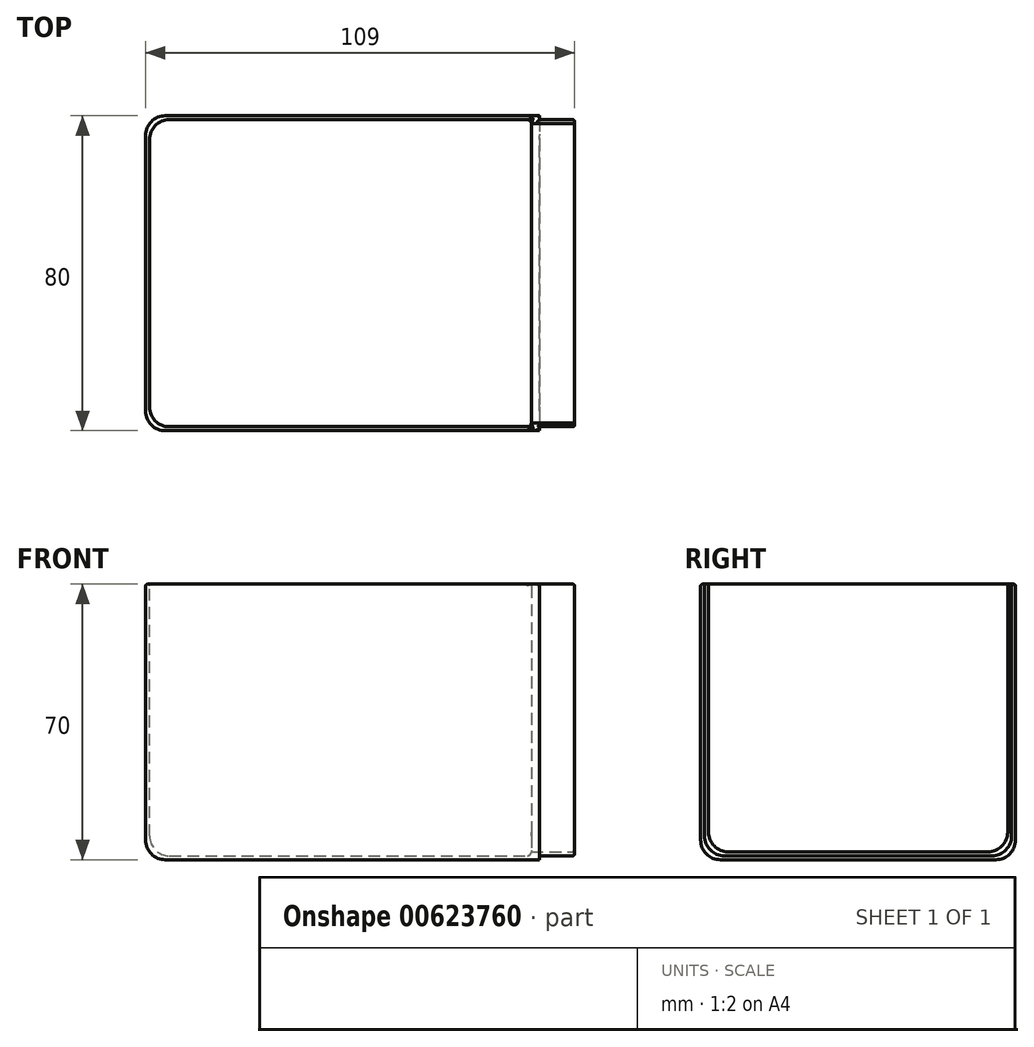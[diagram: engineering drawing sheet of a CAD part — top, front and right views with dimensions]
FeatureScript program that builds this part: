
annotation { "Feature Type Name" : "Feature", "Feature Type Description" : "" }
export const myFeature = defineFeature(function(context is Context, id is Id, definition is map)
    precondition{}
    {
        {
            var Q0;
            Q0=qCreatedBy(makeId("Top.planeOp"),FACE);
            var sketch = newSketch(context, id + "F0", { "sketchPlane" : qUnion([Q0])});
            skLineSegment(sketch, "E0.bottom", {"start": v(50, -40) * mm, "end": v(-50, -40) * mm});
            skLineSegment(sketch, "E0.top", {"start": v(50, 40) * mm, "end": v(-50, 40) * mm});
            skLineSegment(sketch, "E0.left", {"start": v(50, -40) * mm, "end": v(50, 40) * mm});
            skLineSegment(sketch, "E0.right", {"start": v(-50, -40) * mm, "end": v(-50, 40) * mm});
            skPoint(sketch, "E0.middle", {"position": v(0, 0) * mm});
            skSolve(sketch);
        }
        {
            var Q0;
            Q0=makeQuery(id+"F0.imprint","IMPRINT",FACE,{"disambiguationData":[TD([[makeQuery(id+"F0.imprint","IMPRINT",EDGE,{"derivedFrom":sQuery(id+"F0.wireOp",EDGE,"E0.bottom")}),-1.0]])]});
            extrude(context, id + "F1", {"entities" : qUnion([Q0]), "depth" : 70 * mm, "offsetDistance" : 25 * mm});
        }
        {
            var Q0;
            Q0=makeQuery(id+"F1.opExtrude","CAP_FACE",FACE,{"disambiguationData":[OSD([sQuery(id+"F0.wireOp",EDGE,"E0.bottom"),sQuery(id+"F0.wireOp",EDGE,"E0.top"),sQuery(id+"F0.wireOp",EDGE,"E0.left"),sQuery(id+"F0.wireOp",EDGE,"E0.right")])],"isStart":false});
            var sketch = newSketch(context, id + "F2", { "sketchPlane" : qUnion([Q0])});
            skLineSegment(sketch, "E1.bottom", {"start": v(-49, 39) * mm, "end": v(48, 39) * mm});
            skLineSegment(sketch, "E1.top", {"start": v(-49, -39) * mm, "end": v(48, -39) * mm});
            skLineSegment(sketch, "E1.left", {"start": v(-49, 39) * mm, "end": v(-49, -39) * mm});
            skLineSegment(sketch, "E1.right", {"start": v(48, 39) * mm, "end": v(48, -39) * mm});
            skLineSegment(sketch, "E2", {"start": v(-50, 20.59) * mm, "end": v(-49, 20.59) * mm});
            skLineSegment(sketch, "E3", {"start": v(-70.41, 40) * mm, "end": v(-70.41, 39) * mm});
            skLineSegment(sketch, "E4", {"start": v(-57.73, -39) * mm, "end": v(-57.73, -40) * mm});
            skLineSegment(sketch, "E5", {"start": v(48, -31.07) * mm, "end": v(50, -31.07) * mm});
            skSolve(sketch);
        }
        {
            var Q0;
            {var subQ4=sQuery(id+"F2.wireOp",EDGE,"E1.left");var subQ6=sQuery(id+"F2.wireOp",EDGE,"E1.bottom");var subQ9=makeQuery(id+"F2.imprint","INTERSECT",VERTEX,{"derivedFrom":[subQ6,subQ4]});Q0=makeQuery(id+"F2.imprint","IMPRINT",FACE,{"disambiguationData":[TD([[makeQuery(id+"F2.imprint","IMPRINT",EDGE,{"disambiguationData":[TD([[subQ9,-1.0]])],"derivedFrom":subQ6}),-1.0]])]});}
            extrude(context, id + "F3", {"entities" : qUnion([Q0]), "operationType" : NewBodyOperationType.REMOVE, "oppositeDirection" : true, "depth" : 69 * mm, "offsetDistance" : 25 * mm});
        }
        {
            var Q0;
            Q0=makeQuery(id+"F1.opExtrude","SWEPT_FACE",FACE,{"disambiguationData":[OSD([sQuery(id+"F0.wireOp",EDGE,"E0.left")])]});
            var sketch = newSketch(context, id + "F4", { "sketchPlane" : qUnion([Q0])});
            skLineSegment(sketch, "E6.bottom", {"start": v(38, 70) * mm, "end": v(-38, 70) * mm});
            skLineSegment(sketch, "E6.top", {"start": v(38, 2) * mm, "end": v(-38, 2) * mm});
            skLineSegment(sketch, "E6.left", {"start": v(38, 70) * mm, "end": v(38, 2) * mm});
            skLineSegment(sketch, "E6.right", {"start": v(-38, 70) * mm, "end": v(-38, 2) * mm});
            skLineSegment(sketch, "E7", {"start": v(-40, 42.3) * mm, "end": v(-38, 42.3) * mm});
            skSolve(sketch);
        }
        {
            var Q0;
            {var subQ1=sQuery(id+"F4.wireOp",EDGE,"E6.bottom");Q0=makeQuery(id+"F4.imprint","IMPRINT",FACE,{"disambiguationData":[TD([[makeQuery(id+"F4.imprint","IMPRINT",EDGE,{"derivedFrom":subQ1}),-1.0]])]});}
            extrude(context, id + "F5", {"entities" : qUnion([Q0]), "operationType" : NewBodyOperationType.REMOVE, "oppositeDirection" : true, "depth" : 2 * mm, "offsetDistance" : 25 * mm});
        }
        {
            var Q0;
            Q0=makeQuery(id+"F3.boolean.opBoolean","COPY",FACE,{"derivedFrom":makeQuery(id+"F3.opExtrude","SWEPT_FACE",FACE,{"disambiguationData":[OSD([sQuery(id+"F2.wireOp",EDGE,"E1.right")])]})});
            var sketch = newSketch(context, id + "F6", { "sketchPlane" : qUnion([Q0])});
            skSolve(sketch);
        }
        {
            var Q0;
            {var subQ0=sQuery(id+"F2.wireOp",EDGE,"E1.right");Q0=makeQuery(id+"F6.imprint","IMPRINT",FACE,{"disambiguationData":[TD([[makeQuery(id+"F6.imprint","IMPRINT",EDGE,{"derivedFrom":makeQuery(id+"F3.boolean.opBoolean","COPY",EDGE,{"derivedFrom":makeQuery(id+"F3.opExtrude","CAP_EDGE",EDGE,{"disambiguationData":[OSD([subQ0])],"isStart":false})})}),1.0]])]});}
            extrude(context, id + "F7", {"entities" : qUnion([Q0]), "operationType" : NewBodyOperationType.ADD, "oppositeDirection" : true, "depth" : 11 * mm, "offsetDistance" : 25 * mm});
        }
        {
            var Q0;
            Q0=makeQuery(id+"F3.boolean.opBoolean","COPY",EDGE,{"derivedFrom":makeQuery(id+"F3.opExtrude","CAP_EDGE",EDGE,{"disambiguationData":[OSD([sQuery(id+"F2.wireOp",EDGE,"E1.bottom")])],"isStart":false})});
            var Q1;
            Q1=makeQuery(id+"F3.boolean.opBoolean","COPY",EDGE,{"derivedFrom":makeQuery(id+"F3.opExtrude","CAP_EDGE",EDGE,{"disambiguationData":[OSD([sQuery(id+"F2.wireOp",EDGE,"E1.left")])],"isStart":false})});
            var Q2;
            Q2=makeQuery(id+"F3.boolean.opBoolean","COPY",EDGE,{"derivedFrom":makeQuery(id+"F3.opExtrude","CAP_EDGE",EDGE,{"disambiguationData":[OSD([sQuery(id+"F2.wireOp",EDGE,"E1.top")])],"isStart":false})});
            var Q3;
            Q3=makeQuery(id+"F1.opExtrude","CAP_EDGE",EDGE,{"disambiguationData":[OSD([sQuery(id+"F0.wireOp",EDGE,"E0.top")])],"isStart":true});
            var Q4;
            Q4=makeQuery(id+"F1.opExtrude","CAP_EDGE",EDGE,{"disambiguationData":[OSD([sQuery(id+"F0.wireOp",EDGE,"E0.right")])],"isStart":true});
            var Q5;
            Q5=makeQuery(id+"F1.opExtrude","CAP_EDGE",EDGE,{"disambiguationData":[OSD([sQuery(id+"F0.wireOp",EDGE,"E0.bottom")])],"isStart":true});
            var Q6;
            Q6=makeQuery(id+"F1.opExtrude","SWEPT_EDGE",EDGE,{"disambiguationData":[OSD([sQuery(id+"F0.wireOp",EDGE,"E0.bottom"),sQuery(id+"F0.wireOp",EDGE,"E0.right")])]});
            var Q7;
            Q7=makeQuery(id+"F1.opExtrude","SWEPT_EDGE",EDGE,{"disambiguationData":[OSD([sQuery(id+"F0.wireOp",EDGE,"E0.top"),sQuery(id+"F0.wireOp",EDGE,"E0.right")])]});
            var Q8;
            Q8=makeQuery(id+"F3.boolean.opBoolean","COPY",EDGE,{"derivedFrom":makeQuery(id+"F3.opExtrude","SWEPT_EDGE",EDGE,{"disambiguationData":[OSD([sQuery(id+"F2.wireOp",EDGE,"E1.bottom"),sQuery(id+"F2.wireOp",EDGE,"E1.left")])]})});
            var Q9;
            Q9=makeQuery(id+"F3.boolean.opBoolean","COPY",EDGE,{"derivedFrom":makeQuery(id+"F3.opExtrude","SWEPT_EDGE",EDGE,{"disambiguationData":[OSD([sQuery(id+"F2.wireOp",EDGE,"E1.top"),sQuery(id+"F2.wireOp",EDGE,"E1.left")])]})});
            var Q10;
            {var subQ0=sQuery(id+"F2.wireOp",EDGE,"E1.right");var subQ1=sQuery(id+"F2.wireOp",EDGE,"E1.bottom");Q10=makeQuery(id+"F7.opExtrude","SWEPT_EDGE",EDGE,{"disambiguationData":[OSD([subQ1,subQ0]),TDD([makeQuery(id+"F6.imprint","INTERSECT",VERTEX,{"derivedFrom":[makeQuery(id+"F3.boolean.opBoolean","COPY",EDGE,{"derivedFrom":makeQuery(id+"F3.opExtrude","SWEPT_EDGE",EDGE,{"disambiguationData":[OSD([subQ1,subQ0])]})}),makeQuery(id+"F3.boolean.opBoolean","COPY",EDGE,{"derivedFrom":makeQuery(id+"F3.opExtrude","CAP_EDGE",EDGE,{"disambiguationData":[OSD([subQ0])],"isStart":false})})]})])]});}
            var Q11;
            {var subQ0=sQuery(id+"F2.wireOp",EDGE,"E1.right");var subQ1=sQuery(id+"F2.wireOp",EDGE,"E1.top");Q11=makeQuery(id+"F7.opExtrude","SWEPT_EDGE",EDGE,{"disambiguationData":[OSD([subQ1,subQ0]),TDD([makeQuery(id+"F6.imprint","INTERSECT",VERTEX,{"derivedFrom":[makeQuery(id+"F3.boolean.opBoolean","COPY",EDGE,{"derivedFrom":makeQuery(id+"F3.opExtrude","SWEPT_EDGE",EDGE,{"disambiguationData":[OSD([subQ1,subQ0])]})}),makeQuery(id+"F3.boolean.opBoolean","COPY",EDGE,{"derivedFrom":makeQuery(id+"F3.opExtrude","CAP_EDGE",EDGE,{"disambiguationData":[OSD([subQ0])],"isStart":false})})]})])]});}
            var Q12;
            {var subQ0=sQuery(id+"F4.wireOp",EDGE,"E6.right");var subQ1=sQuery(id+"F4.wireOp",EDGE,"E6.top");Q12=makeQuery(id+"F7.boolean.opBoolean","MERGE",EDGE,{"derivedFrom":[makeQuery(id+"F5.boolean.opBoolean","COPY",EDGE,{"derivedFrom":makeQuery(id+"F5.opExtrude","SWEPT_EDGE",EDGE,{"disambiguationData":[OSD([subQ1,subQ0])]})}),makeQuery(id+"F7.opExtrude","SWEPT_EDGE",EDGE,{"disambiguationData":[OSD([subQ1,subQ0])]})]});}
            var Q13;
            {var subQ0=sQuery(id+"F4.wireOp",EDGE,"E6.left");var subQ1=sQuery(id+"F4.wireOp",EDGE,"E6.top");Q13=makeQuery(id+"F7.boolean.opBoolean","MERGE",EDGE,{"derivedFrom":[makeQuery(id+"F5.boolean.opBoolean","COPY",EDGE,{"derivedFrom":makeQuery(id+"F5.opExtrude","SWEPT_EDGE",EDGE,{"disambiguationData":[OSD([subQ1,subQ0])]})}),makeQuery(id+"F7.opExtrude","SWEPT_EDGE",EDGE,{"disambiguationData":[OSD([subQ1,subQ0])]})]});}
            fillet(context, id + "F8", {"entities" : qUnion([Q0, Q1, Q2, Q3, Q4, Q5, Q6, Q7, Q8, Q9, Q10, Q11, Q12, Q13]), "radius" : 5 * mm, "tangentPropagation" : true, "allowEdgeOverflow" : false});
        }
        {
            var Q0;
            {var subQ0=makeQuery(id+"F1.opExtrude","CAP_FACE",FACE,{"disambiguationData":[OSD([sQuery(id+"F0.wireOp",EDGE,"E0.bottom"),sQuery(id+"F0.wireOp",EDGE,"E0.top"),sQuery(id+"F0.wireOp",EDGE,"E0.left"),sQuery(id+"F0.wireOp",EDGE,"E0.right")])],"isStart":false});var subQ1=sQuery(id+"F2.wireOp",EDGE,"E1.right");var subQ3=makeQuery(id+"F3.boolean.opBoolean","COPY",EDGE,{"derivedFrom":makeQuery(id+"F3.opExtrude","CAP_EDGE",EDGE,{"disambiguationData":[OSD([subQ1])],"isStart":true})});Q0=makeQuery(id+"F7.boolean.opBoolean","MERGE",FACE,{"derivedFrom":[subQ0,makeQuery(id+"F7.opExtrude","SWEPT_FACE",FACE,{"disambiguationData":[OSD([subQ1]),TDD([makeQuery(id+"F6.imprint","IMPRINT",EDGE,{"derivedFrom":makeQuery(id+"F5.boolean.opBoolean","SPLIT",EDGE,{"disambiguationData":[TD([makeQuery(id+"F3.boolean.opBoolean","COPY",FACE,{"derivedFrom":makeQuery(id+"F3.opExtrude","SWEPT_FACE",FACE,{"disambiguationData":[OSD([sQuery(id+"F2.wireOp",EDGE,"E1.bottom")])]})})])],"derivedFrom":subQ3})})])]}),makeQuery(id+"F7.opExtrude","SWEPT_FACE",FACE,{"disambiguationData":[OSD([subQ1]),TDD([makeQuery(id+"F6.imprint","IMPRINT",EDGE,{"derivedFrom":makeQuery(id+"F5.boolean.opBoolean","SPLIT",EDGE,{"disambiguationData":[TD([makeQuery(id+"F3.boolean.opBoolean","COPY",FACE,{"derivedFrom":makeQuery(id+"F3.opExtrude","SWEPT_FACE",FACE,{"disambiguationData":[OSD([sQuery(id+"F2.wireOp",EDGE,"E1.top")])]})})])],"derivedFrom":subQ3})})])]})]});}
            var Q1;
            Q1=makeQuery(id+"F7.opExtrude","CAP_FACE",FACE,{"disambiguationData":[OSD([sQuery(id+"F2.wireOp",EDGE,"E1.bottom"),sQuery(id+"F2.wireOp",EDGE,"E1.top"),sQuery(id+"F2.wireOp",EDGE,"E1.right"),sQuery(id+"F4.wireOp",EDGE,"E6.top"),sQuery(id+"F4.wireOp",EDGE,"E6.left"),sQuery(id+"F4.wireOp",EDGE,"E6.right")])],"isStart":false});
            fillet(context, id + "F9", {"entities" : qUnion([Q0, Q1]), "radius" : .5 * mm, "tangentPropagation" : true, "allowEdgeOverflow" : false});
        }
        {
            var Q0;
            Q0=makeQuery(id+"F3.boolean.opBoolean","COPY",EDGE,{"derivedFrom":makeQuery(id+"F3.opExtrude","CAP_EDGE",EDGE,{"disambiguationData":[OSD([sQuery(id+"F2.wireOp",EDGE,"E1.right")])],"isStart":false})});
            fillet(context, id + "F10", {"entities" : qUnion([Q0]), "radius" : 1 * mm, "tangentPropagation" : true, "allowEdgeOverflow" : false});
        }
    });
